# Revit family: ElectricalFixture_WiringAccessories_Hager_Sollysta_PartM_SwitchedRedFusedConnectionUnits
name_source: partatom
category: Electrical Fixtures
revit_build: Autodesk Revit 2015 (Build: 20160512_1515(x64)
units: mm (PartAtom-declared; Revit-internal decimal feet)

## types (2) — shared parameters
CE Approval = Yes
Colour = PartMRed
Default Elevation = 1219.2 mm  [stored 4 ft]
Design Country = China
Expected Life = 25 years
Extrusion From Wall = 11.9 mm
FaceMaterial = Urea Formaldehyde Thermoset Plastic
Features = 13AFCUSwitchedWithRedRocker
Finish = Gloss
Flex Outlet = No
Frequency = 50/60Hz
Gross Weight kg = 0.165
LED Indicator Switch = No
Manufacturer = Hager
Manufacturer Country = United Kingdom
Manufacturer Website = http://www.hager.co.uk
Overall Depth = 26.1 mm
Overall Height = 86 mm  [stored 0.282152 ft]
Overall Length = 86 mm  [stored 0.282152 ft]
Overall Width = 86 mm  [stored 0.282152 ft]
Packaging Recyclable = Yes
Product Family = PartMFusedConnectionUnits
Product Group = WiringAccessories
Product Literature = http://www.hager.co.uk
Product Range = Sollysta
Product URL = http://www.hager.co.uk
Reference Standard = BS 1363-2
RockerMaterial = Hager_RedPartM
Shape = Rectangular
Shipping Weight kg = 0.188
Supply Phase = 1
Switch = Yes
Type = ElectricalFixture
Voltage (Volts) = 230V/240V

## per-type parameters (varying)
| type | Description | EAN Code | Material | Name | Technical Description |
| WMSSU83R | 13AFCUSwitchedWithRedRocker | 5015654759629 | Urea Formaldehyde Thermoset Plastic | PartMFusedConnectionUnits_WMSSU83R | 13AFCUSwitchedWithRedRocker |
| WMSSU83RR | 13AFCUSwitchedWithRedFacePlate&Rocker | 5015654759636 | Hager_RedPartM | PartMFusedConnectionUnits_WMSSU83RR | 13AFCUSwitchedWithRedFacePlate&Rocker |

note: column(s) folded — value = type name in every type: Product Model Number, Unique Reference

note: [stored X ft] marks values corroborated as IEEE doubles in the binary element streams (Revit-internal decimal feet)

## geometry (parser evidence)
native form markers: Blend x4, Sweep x3
no freeform markers — native parametric forms only
